# Revit family: EU_SINGLE_IDU_360_CST_L+_Ver.1.1
name_source: partatom
category: Mechanical Equipment
revit_build: Autodesk Revit 2016 (Build: 20150220_1215(x64)
units: mm (PartAtom-declared; Revit-internal decimal feet)

## family parameters
Always vertical = Yes
Cut with Voids When Loaded = No
OmniClass Number = 23.75.00.00
OmniClass Title = Climate Control (HVAC)
Part Type = Normal
Room Calculation Point = No
Round Connector Dimension = Use Diameter
Shared = No
Work Plane-Based = No

## types (20) — shared parameters
Designation = -
Free Content Downloads = -
Manufacturer = SAMSUNG
Manufacturer Metadata = -
Motor Output = 97 W
Notes = -
Product Documentation Link = -
Product Page URL = -
Sales Rep Locator = -
Serial Number = -
Subscribe for Update Alerts = -
System Served = -
URL = www.samsung.com

## per-type parameters (varying)
| type | Circle | Model | Net Weight | Panel Model | Panel Net Weight | Refrigerant Type | Square |
| 9.00 kW,  220-240V, 360 CASSETTE (Circle) | Yes | AC090MN4PKH/EU | 23.50 kg | PC4NUNMAN | 2.70 kg | R410A | No |
| 9.00 kW,  220-240V, 360 CASSETTE (Square) | No | AC090MN4PKH/EU | 23.50 kg | PC4NUDMAN | 3.60 kg | R410A | Yes |
| 10.00 kW,  220-240V, 360 CASSETTE (Circle) | Yes | AC100MN4PKH/EU | 23.50 kg | PC4NUNMAN | 2.70 kg | R410A | No |
| 10.00 kW,  220-240V, 360 CASSETTE (Square) | No | AC100MN4PKH/EU | 23.50 kg | PC4NUDMAN | 3.60 kg | R410A | Yes |
| 12.00 kW,  220-240V, 360 CASSETTE (Circle) | Yes | AC120MN4PKH/EU | 23.50 kg | PC4NUNMAN | 2.70 kg | R410A | No |
| 12.00 kW,  220-240V, 360 CASSETTE (Square) | No | AC120MN4PKH/EU | 23.50 kg | PC4NUDMAN | 3.60 kg | R410A | Yes |
| 13.40 kW,  220-240V, 360 CASSETTE (Circle) | Yes | AC140MN4PKH/EU | 25.50 kg | PC4NUNMAN | 2.70 kg | R410A | No |
| 13.40 kW,  220-240V, 360 CASSETTE (Square) | No | AC140MN4PKH/EU | 25.50 kg | PC4NUDMAN | 3.60 kg | R410A | Yes |
| 10.0 kW, 220-240V, 360 Cassette, R32, 1phase ODU(Square) | No | AC100RN4PKG/EU | 23.50 kg | PC4NUDMAN | 3.60 kg | R32 | Yes |
| 10.0 kW, 220-240V, 360 Cassette, R32, 1phase ODU(Circle) | Yes | AC100RN4PKG/EU | 23.50 kg | PC4NUDMAN | 3.60 kg | R32 | No |
| 10.0 kW, 220-240V, 360 Cassette, R32, 3phase ODU(Square) | No | AC100RN4PKG/EU | 23.50 kg | PC4NUDMAN | 3.60 kg | R32 | Yes |
| 10.0 kW, 220-240V, 360 Cassette, R32, 3phase ODU(Circle) | Yes | AC100RN4PKG/EU | 23.50 kg | PC4NUDMAN | 3.60 kg | R32 | No |
| 12.0 kW, 220-240V, 360 Cassette, R32, 1phase ODU(Circle) | Yes | AC120RN4PKG/EU | 23.50 kg | PC4NUDMAN | 3.60 kg | R32 | No |
| 12.0 kW, 220-240V, 360 Cassette, R32, 1phase ODU(Square) | No | AC120RN4PKG/EU | 23.50 kg | PC4NUDMAN | 3.60 kg | R32 | Yes |
| 12.0 kW, 220-240V, 360 Cassette, R32, 3phase ODU(Circle) | Yes | AC120RN4PKG/EU | 23.50 kg | PC4NUDMAN | 3.60 kg | R32 | No |
| 12.0 kW, 220-240V, 360 Cassette, R32, 3phase ODU(Square) | No | AC120RN4PKG/EU | 23.50 kg | PC4NUDMAN | 3.60 kg | R32 | Yes |
| 14.0 kW, 220-240V, 360 Cassette, R32, 1phase ODU(Circle) | Yes | AC140RN4PKG/EU | 25.50 kg | PC4NUDMAN | 3.60 kg | R32 | No |
| 14.0 kW, 220-240V, 360 Cassette, R32, 1phase ODU(Square) | No | AC140RN4PKG/EU | 25.50 kg | PC4NUDMAN | 3.60 kg | R32 | Yes |
| 14.0 kW, 220-240V, 360 Cassette, R32, 3phase ODU(Circle) | Yes | AC140RN4PKG/EU | 25.50 kg | PC4NUDMAN | 3.60 kg | R32 | No |
| 14.0 kW, 220-240V, 360 Cassette, R32, 3phase ODU(Square) | No | AC140RN4PKG/EU | 25.50 kg | PC4NUDMAN | 3.60 kg | R32 | Yes |

## geometry (parser evidence)
native form markers: Sweep x3
no freeform markers — native parametric forms only
